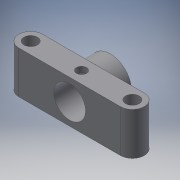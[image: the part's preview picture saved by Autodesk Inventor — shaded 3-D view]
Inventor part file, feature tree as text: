
AUTODESK INVENTOR PART (.ipt)
format: ipt  version: 2016 (Build 200138000, 138)  size: 133,120 bytes
history: native  units: mm
features: extrude x4, sketch x4, projected_geometry x1
ambient origin geometry x8: Origin, YZ Plane, XZ Plane, XY Plane, X Axis, Y Axis, Z Axis, Center Point
bodies: Solid1 (feature_tree)
feature tree (9):
  extrude  "Extrusion1"  Depth=8.0mm
  extrude  "Extrusion2"  Depth=25.0mm TaperAngle=0.0deg
  extrude  "Extrusion3"  Depth=25.0mm TaperAngle=0.0deg
  extrude  "Extrusion4"  Depth=10.0mm
  sketch  "Sketch1"  dims[d0=60.0mm d1=8.0mm]
  sketch  "Sketch2"  dims[d2=7.0mm d3=25.0mm d4=0.0mm]
  projected_geometry  "Projected Loop1"
  sketch  "Sketch3"  dims[d5=18.75mm d6=25.0mm d7=0.0mm]
  sketch  "Sketch4"  dims[d8=10.0mm d9=0.0mm d10=6.0mm d11=10.0mm d12=0.0mm]
